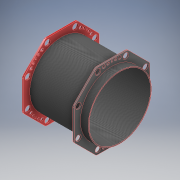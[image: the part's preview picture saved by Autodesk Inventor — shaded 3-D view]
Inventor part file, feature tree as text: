
AUTODESK INVENTOR PART (.ipt)
format: ipt  version: 2022 (Build 260153000, 153)  size: 319,488 bytes
history: native  units: mm
features: hole x8, sketch x7, extrude x5, plane x2, fillet x2, other x2
ambient origin geometry x8: Origin, YZ Plane, XZ Plane, XY Plane, X Axis, Y Axis, Z Axis, Center Point
bodies: Solid1 (feature_tree)
feature tree (26):
  extrude  "Extrusion1"  Depth=370.0mm
  sketch  "Sketch2"  dims[d3=370.0mm d4=0.0mm d5=8.0mm d6=0.0mm]
  extrude  "Extrusion2"  Depth=8.0mm TaperAngle=0.0deg
  plane  "Work Plane1"
  sketch  "Sketch4"  dims[d11=8.0mm d12=0.0mm d13=20.0mm]
  extrude  "BackPlate"  [1 undecoded]
  fillet  "Fillet1"  Radius=8.0mm
  plane  "Work Plane3"
  extrude  "FrontPlate"  Depth=20.0mm
  extrude  "Extrusion5"  [1 undecoded]
  fillet  "Fillet2"  [1 undecoded]
  other  "BackplateHoles"
  other  "FrontplateHoles"
  hole  "Hole1"  [1 undecoded]
  hole  "Hole2"  [1 undecoded]
  hole  "Hole3"  [1 undecoded]
  hole  "Hole4"  [1 undecoded]
  hole  "Hole5"  [1 undecoded]
  hole  "Hole6"  [1 undecoded]
  hole  "Hole7"  [1 undecoded]
  hole  "Hole8"  [1 undecoded]
  sketch  "Sketch1"  dims[d0=370.0mm d1=0.0mm d2=390.0mm]
  sketch  "Sketch3"  dims[d7=20.0mm d8=-328.0mm d9=8.0mm d10=0.0mm]
  sketch  "Sketch5"  dims[d16=36.0mm d17=6.0mm d18=4.0mm d19=2.0mm d20=90.0deg d21=20.0mm d22=20.594885mm]
  sketch  "Sketch6"  dims[d23=20.0mm d24=6.0mm d25=4.0mm d26=2.0mm d27=90.0deg d28=8.0mm d29=20.594885mm]
  sketch  "Sketch7"  dims[d30=16.0mm d31=6.0mm d32=4.0mm d33=2.0mm d34=90.0deg d35=8.0mm d36=20.594885mm d37=12.0mm d38=6.0mm d39=4.0mm d40=2.0mm d41=90.0deg d42=8.0mm d43=20.594885mm d44=36.0mm d45=6.0mm d46=4.0mm d47=2.0mm d48=90.0deg d49=8.0mm d50=20.594885mm d51=20.0mm d52=6.0mm d53=4.0mm d54=2.0mm d55=90.0deg d56=8.0mm d57=20.594885mm d58=16.0mm d59=6.0mm d60=4.0mm d61=2.0mm d62=90.0deg d63=8.0mm d64=20.594885mm d65=12.0mm d66=6.0mm d67=4.0mm d68=2.0mm d69=90.0deg d70=8.0mm d71=20.594885mm]
note: 11 required parameter values undecoded (feature->parameter linkage not recoverable at this tier; creation-order binding heuristic only, values carry confidence <= 0.55)
